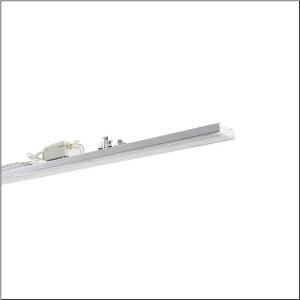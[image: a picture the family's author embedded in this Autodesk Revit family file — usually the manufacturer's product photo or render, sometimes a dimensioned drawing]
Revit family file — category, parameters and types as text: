
# Revit family: licross_21_recessed_mo_52te18dn495g
name_source: partatom
category: Lighting Fixtures
units: mm (PartAtom-declared; Revit-internal decimal feet)

## family parameters
Cut with Voids When Loaded = No
Host = Face
Light Source = No
Part Type = Normal
Room Calculation Point = No
Round Connector Dimension = Use Diameter
Shared = No

## types (1)
- --- (1 x LED, 9990 lm, 58 W, 4000K)
    Apparent Load = 58 VA
    CIE Flux Codes = 79 95 99 100 100
    Color Rendering = 80
    Color Temperature = 4000K
    Default Elevation = 1800 mm
    Description = Licross 21 Recessed MO, luminaire insert, of sheet steel, galvanised, coil coated, white, length: 1.500mm, width: 66mm, height: 67mm, LED rated luminous flux: 9.990lm, light colour: 840, SDCM (Standard Deviation of Colour Matching)MacAdam ≤ 3 SDCM (initial), control gear: DALI 2, with plug, 5-pole, with phase selection, mains connection: 220..240V, AC, 50/60Hz, rated input power: 58W, internal wiring halogen-free, primary light control with lens, of plastic, primary optical cover: cover, of PMMA, light emission: direct distribution, primary light characteristic: symmetric, protection rating (complete): IP54, insulation class (complete): insulation class I (protective earthing), certification: CE, ENEC, VDE, UKCA, protection symbol: D if used in an environment with non-conductive dust loads with corresponding accessories, impact resistance: IK06, permissible ambient temperature for indoor applications: -25..+35°C, corresponds to IFS (International Featured Standards) requirements for safety and quality in the food industry, reducing of maximum allowable ambient temperature of 5°C with ceiling mounting, LABS conformity tested according to VDMA 24364:2018-05, The light source and the operating device comply with the requirements of the Ecodesign Regulation (EU) 2019/2020 and are replaceable in accordance with this regulation, packaging unit: 1 piece
    Height = 58 mm
    Lamp = 1 x LED
    Lamp Light Flux = 9990 lm
    Lamp Power = 58 W
    Lamp count = 1
    Length = 1500 mm
    Luminous efficacy = 172 lm/W
    Manufacturer = Siteco
    ModVariant = No
    Model = 52TE18DN495G
    Mounting Place = Ceiling
    Mounting Type = Pendant
    Number of Poles = 1
    OnlyDefault = Yes
    Power Factor = 1
    Product Name = Licross 21 Recessed MO
    Product group = luminaire insert | ceiling pendant
    ProductGroupID = 901
    Protection Class = Protection class I
    Protection Degree = IP 54
    RLX_Detail_Level = 1
    RLX_Emergency_Light_Flux = 0 lm
    RLX_Emergency_Type = 0
    RLX_Emergency_Type_DB = No
    RlxData = <blob elided: 24789 chars, md5=0cac0d2c>
    Socket = socket
    Standby Power = 0 W
    System Light Flux = 9990 lm
    System Power = 58 W
    Type Comments = factory setting: luminous flux: 100 % | dim-lin: 254 | 390 mA
    Type Image = l_1296930.jpg
    URL = http://relux.com
    VarID = @adj_127647
    Voltage = 0 V
    Weight = 0.00 kg
    Width = 66 mm

## geometry (parser evidence)
native form markers: Blend x4, Sweep x12
no freeform markers — native parametric forms only
